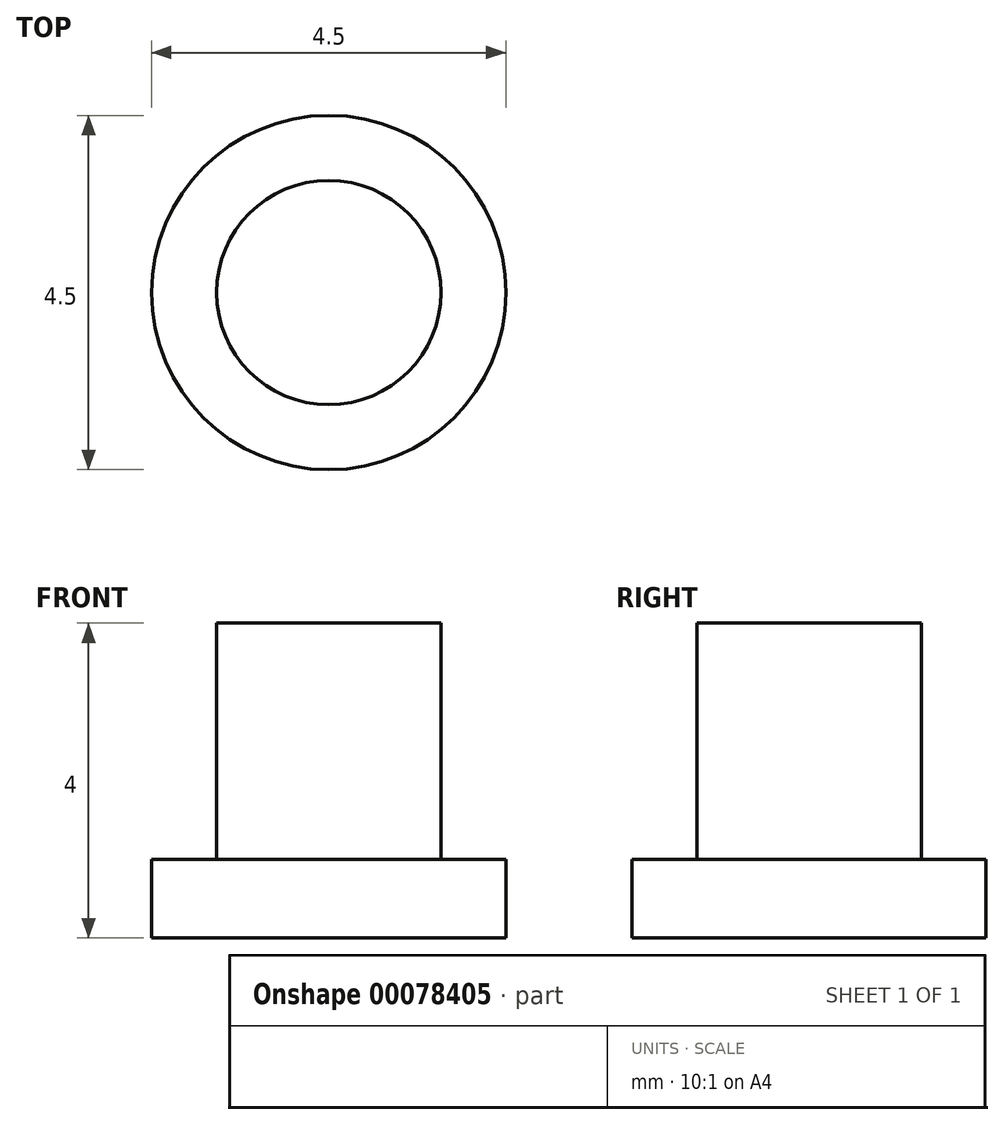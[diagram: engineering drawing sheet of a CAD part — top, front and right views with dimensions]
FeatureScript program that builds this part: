
annotation { "Feature Type Name" : "Feature", "Feature Type Description" : "" }
export const myFeature = defineFeature(function(context is Context, id is Id, definition is map)
    precondition{}
    {
        {
            var Q0;
            Q0=qCreatedBy(makeId("Top.planeOp"),FACE);
            var sketch = newSketch(context, id + "F0", { "sketchPlane" : qUnion([Q0])});
            skCircle(sketch, "E0", {"center": v(0, 0) * mm, "radius": 2.25 * mm});
            skSolve(sketch);
        }
        {
            var Q0;
            Q0=makeQuery(id+"F0.imprint","IMPRINT",FACE,{"disambiguationData":[TD([[makeQuery(id+"F0.imprint","IMPRINT",EDGE,{"derivedFrom":sQuery(id+"F0.wireOp",EDGE,"E0")}),1.0]])]});
            extrude(context, id + "F1", {"entities" : qUnion([Q0]), "depth" : 1 * mm, "offsetDistance" : 25 * mm});
        }
        {
            var Q0;
            Q0=makeQuery(id+"F1.opExtrude","CAP_FACE",FACE,{"disambiguationData":[OSD([sQuery(id+"F0.wireOp",EDGE,"E0")])],"isStart":false});
            var sketch = newSketch(context, id + "F2", { "sketchPlane" : qUnion([Q0])});
            skCircle(sketch, "E1", {"center": v(0, 0) * mm, "radius": 1.42 * mm});
            skSolve(sketch);
        }
        {
            var Q0;
            Q0 = qSketchRegion(id + "F2", true);
            extrude(context, id + "F3", {"entities" : qUnion([Q0]), "operationType" : NewBodyOperationType.ADD, "depth" : 3 * mm, "offsetDistance" : 25 * mm});
        }
    });
